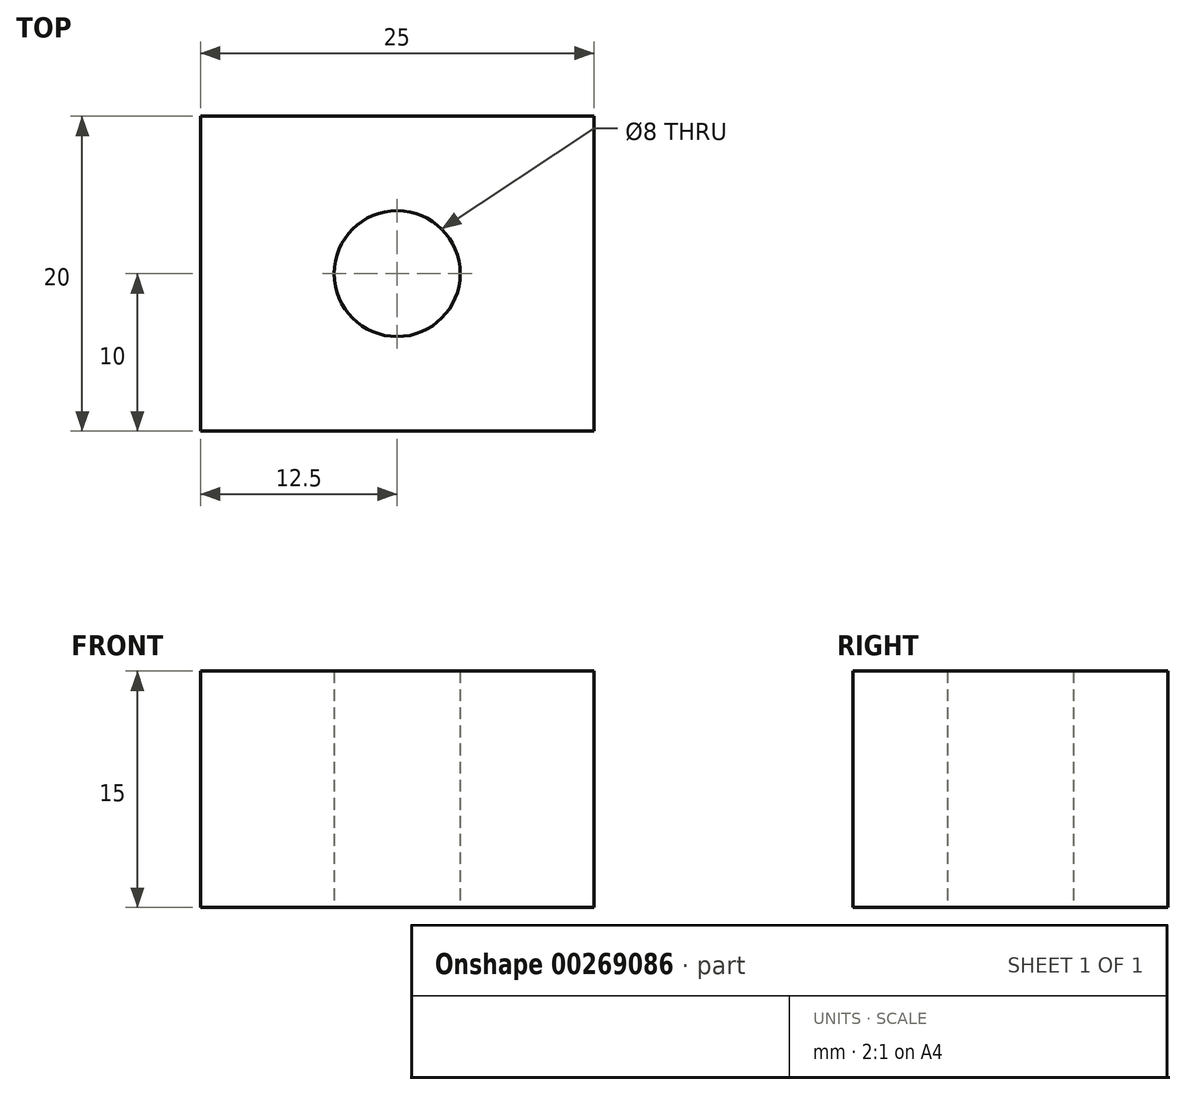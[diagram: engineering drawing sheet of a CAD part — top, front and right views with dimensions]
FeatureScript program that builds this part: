
annotation { "Feature Type Name" : "Feature", "Feature Type Description" : "" }
export const myFeature = defineFeature(function(context is Context, id is Id, definition is map)
    precondition{}
    {
        {
            var Q0;
            Q0=qCreatedBy(makeId("Top.planeOp"),FACE);
            var sketch = newSketch(context, id + "F0", { "sketchPlane" : qUnion([Q0])});
            skLineSegment(sketch, "E0.bottom", {"start": v(0, 0) * mm, "end": v(25, 0) * mm});
            skLineSegment(sketch, "E0.top", {"start": v(0, 20) * mm, "end": v(25, 20) * mm});
            skLineSegment(sketch, "E0.left", {"start": v(0, 0) * mm, "end": v(0, 20) * mm});
            skLineSegment(sketch, "E0.right", {"start": v(25, 0) * mm, "end": v(25, 20) * mm});
            skCircle(sketch, "E1", {"center": v(12.5, 10) * mm, "radius": 4 * mm});
            skLineSegment(sketch, "E2", {"start": v(12.5, 20) * mm, "end": v(12.5, 10) * mm, "construction": true});
            skLineSegment(sketch, "E3", {"start": v(0, 10) * mm, "end": v(12.5, 10) * mm, "construction": true});
            skSolve(sketch);
        }
        {
            var Q0;
            Q0=makeQuery(id+"F0.imprint","IMPRINT",FACE,{"disambiguationData":[TD([[makeQuery(id+"F0.imprint","IMPRINT",EDGE,{"derivedFrom":sQuery(id+"F0.wireOp",EDGE,"E0.bottom")}),1.0]])]});
            extrude(context, id + "F1", {"entities" : qUnion([Q0]), "depth" : 15 * mm});
        }
    });
